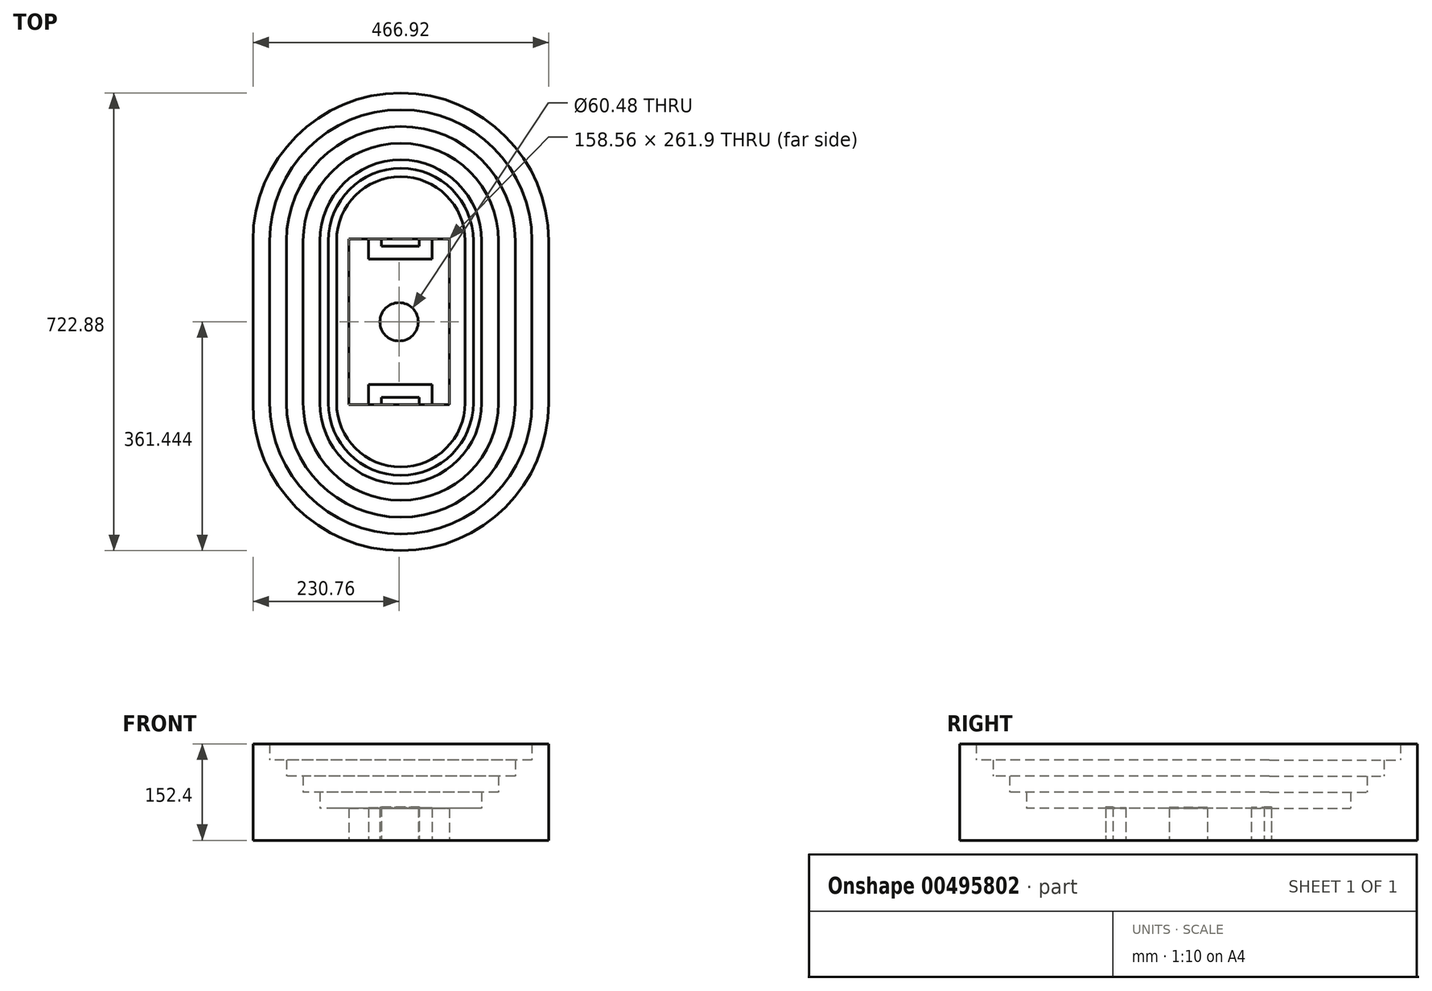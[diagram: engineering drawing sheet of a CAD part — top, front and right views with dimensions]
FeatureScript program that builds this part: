
annotation { "Feature Type Name" : "Feature", "Feature Type Description" : "" }
export const myFeature = defineFeature(function(context is Context, id is Id, definition is map)
    precondition{}
    {
        {
            var Q0;
            Q0=qCreatedBy(makeId("Top.planeOp"),FACE);
            var sketch = newSketch(context, id + "F0", { "sketchPlane" : qUnion([Q0])});
            skLineSegment(sketch, "E0.bottom", {"start": v(-59.16, 165.76) * mm, "end": v(99.4, 165.76) * mm});
            skLineSegment(sketch, "E0.top", {"start": v(-59.16, -96.14) * mm, "end": v(99.4, -96.14) * mm});
            skLineSegment(sketch, "E0.left", {"start": v(-59.16, 165.76) * mm, "end": v(-59.16, -96.14) * mm});
            skLineSegment(sketch, "E0.right", {"start": v(99.4, 165.76) * mm, "end": v(99.4, -96.14) * mm});
            skLineSegment(sketch, "E1.1", {"start": v(124.12, 162.8) * mm, "end": v(124.12, -93.16) * mm});
            skLineSegment(sketch, "E1.3", {"start": v(-78.49, 162.8) * mm, "end": v(-78.49, -93.16) * mm});
            skArc(sketch, "E2", {"start": v(124.12, 162.8) * mm, "mid": v(22.82, 264.1) * mm, "end": v(-78.49, 162.8) * mm});
            skArc(sketch, "E3", {"start": v(-78.49, -93.16) * mm, "mid": v(22.82, -194.47) * mm, "end": v(124.12, -93.16) * mm});
            skArc(sketch, "E4.0", {"start": v(137.34, 162.8) * mm, "mid": v(22.82, 277.31) * mm, "end": v(-91.7, 162.8) * mm});
            skLineSegment(sketch, "E4.1", {"start": v(137.34, 162.8) * mm, "end": v(137.34, -93.16) * mm});
            skArc(sketch, "E4.2", {"start": v(-91.7, -93.16) * mm, "mid": v(22.82, -207.68) * mm, "end": v(137.34, -93.16) * mm});
            skLineSegment(sketch, "E4.3", {"start": v(-91.7, 162.8) * mm, "end": v(-91.7, -93.16) * mm});
            skArc(sketch, "E5.0", {"start": v(150.55, 162.8) * mm, "mid": v(22.82, 290.53) * mm, "end": v(-104.92, 162.8) * mm});
            skLineSegment(sketch, "E5.1", {"start": v(150.55, 162.8) * mm, "end": v(150.55, -93.16) * mm});
            skArc(sketch, "E5.2", {"start": v(-104.92, -93.16) * mm, "mid": v(22.82, -220.9) * mm, "end": v(150.55, -93.16) * mm});
            skLineSegment(sketch, "E5.3", {"start": v(-104.92, 162.8) * mm, "end": v(-104.92, -93.16) * mm});
            skArc(sketch, "E6.0", {"start": v(176.98, 162.8) * mm, "mid": v(22.82, 316.96) * mm, "end": v(-131.35, 162.8) * mm});
            skLineSegment(sketch, "E6.1", {"start": v(176.98, 162.8) * mm, "end": v(176.98, -93.16) * mm});
            skArc(sketch, "E6.2", {"start": v(-131.35, -93.16) * mm, "mid": v(22.82, -247.33) * mm, "end": v(176.98, -93.16) * mm});
            skLineSegment(sketch, "E6.3", {"start": v(-131.35, 162.8) * mm, "end": v(-131.35, -93.16) * mm});
            skArc(sketch, "E7.0", {"start": v(203.42, 162.8) * mm, "mid": v(22.82, 343.4) * mm, "end": v(-157.78, 162.8) * mm});
            skLineSegment(sketch, "E7.1", {"start": v(203.42, 162.8) * mm, "end": v(203.42, -93.16) * mm});
            skArc(sketch, "E7.2", {"start": v(-157.78, -93.16) * mm, "mid": v(22.82, -273.76) * mm, "end": v(203.42, -93.16) * mm});
            skLineSegment(sketch, "E7.3", {"start": v(-157.78, 162.8) * mm, "end": v(-157.78, -93.16) * mm});
            skArc(sketch, "E8.0", {"start": v(229.85, 162.8) * mm, "mid": v(22.82, 369.82) * mm, "end": v(-184.21, 162.8) * mm});
            skLineSegment(sketch, "E8.1", {"start": v(229.85, 162.8) * mm, "end": v(229.85, -93.16) * mm});
            skArc(sketch, "E8.2", {"start": v(-184.21, -93.16) * mm, "mid": v(22.82, -300.2) * mm, "end": v(229.85, -93.16) * mm});
            skLineSegment(sketch, "E8.3", {"start": v(-184.21, 162.8) * mm, "end": v(-184.21, -93.16) * mm});
            skArc(sketch, "E9.0", {"start": v(256.28, 162.8) * mm, "mid": v(22.82, 396.25) * mm, "end": v(-210.64, 162.8) * mm});
            skLineSegment(sketch, "E9.1", {"start": v(256.28, 162.8) * mm, "end": v(256.28, -93.16) * mm});
            skArc(sketch, "E9.2", {"start": v(-210.64, -93.16) * mm, "mid": v(22.82, -326.63) * mm, "end": v(256.28, -93.16) * mm});
            skLineSegment(sketch, "E9.3", {"start": v(-210.64, 162.8) * mm, "end": v(-210.64, -93.16) * mm});
            skLineSegment(sketch, "E10", {"start": v(-59.16, 34.81) * mm, "end": v(99.4, 34.81) * mm});
            skCircle(sketch, "E11", {"center": v(20.12, 34.81) * mm, "radius": 30.24 * mm});
            skLineSegment(sketch, "E12", {"start": v(22.82, -96.14) * mm, "end": v(-27.98, -96.14) * mm});
            skLineSegment(sketch, "E13", {"start": v(22.82, -96.14) * mm, "end": v(67.85, -96.14) * mm});
            skLineSegment(sketch, "E14", {"start": v(-27.98, 165.76) * mm, "end": v(72.35, 165.76) * mm});
            skLineSegment(sketch, "E15", {"start": v(72.35, -96.14) * mm, "end": v(22.82, -96.14) * mm});
            skLineSegment(sketch, "E16", {"start": v(-27.98, -96.14) * mm, "end": v(-27.98, -64.39) * mm});
            skLineSegment(sketch, "E17", {"start": v(72.35, -96.14) * mm, "end": v(72.35, -64.39) * mm});
            skLineSegment(sketch, "E18", {"start": v(72.35, -64.39) * mm, "end": v(-27.98, -64.39) * mm});
            skLineSegment(sketch, "E19", {"start": v(-27.98, 165.76) * mm, "end": v(-27.98, 134.01) * mm});
            skLineSegment(sketch, "E20", {"start": v(-27.98, 134.01) * mm, "end": v(72.35, 134.01) * mm});
            skLineSegment(sketch, "E21", {"start": v(72.35, 134.01) * mm, "end": v(72.35, 165.76) * mm});
            skLineSegment(sketch, "E22.0", {"start": v(-7.66, -96.14) * mm, "end": v(-7.66, -84.7) * mm});
            skLineSegment(sketch, "E22.1", {"start": v(52.03, -84.7) * mm, "end": v(-7.66, -84.7) * mm});
            skLineSegment(sketch, "E22.2", {"start": v(52.03, -94.87) * mm, "end": v(52.03, -84.7) * mm});
            skLineSegment(sketch, "E23.0", {"start": v(52.03, 154.33) * mm, "end": v(52.03, 165.76) * mm});
            skLineSegment(sketch, "E23.1", {"start": v(-7.66, 154.33) * mm, "end": v(52.03, 154.33) * mm});
            skLineSegment(sketch, "E23.2", {"start": v(-7.66, 165.76) * mm, "end": v(-7.66, 154.33) * mm});
            skLineSegment(sketch, "E24", {"start": v(52.03, -94.87) * mm, "end": v(52.03, -96.14) * mm});
            skSolve(sketch);
        }
        {
            var Q0;
            {var subQ0=sQuery(id+"F0.wireOp",EDGE,"E23.0");Q0=makeQuery(id+"F0.imprint","IMPRINT",FACE,{"disambiguationData":[TD([[makeQuery(id+"F0.imprint","IMPRINT",EDGE,{"derivedFrom":subQ0}),1.0]])]});}
            var Q1;
            {var subQ0=sQuery(id+"F0.wireOp",EDGE,"E22.0");Q1=makeQuery(id+"F0.imprint","IMPRINT",FACE,{"disambiguationData":[TD([[makeQuery(id+"F0.imprint","IMPRINT",EDGE,{"derivedFrom":subQ0}),-1.0]])]});}
            extrude(context, id + "F1", {"entities" : qUnion([Q0, Q1]), "depth" : 53.34 * mm});
        }
        {
            var Q0;
            {var subQ0=sQuery(id+"F0.wireOp",EDGE,"E16");Q0=makeQuery(id+"F0.imprint","IMPRINT",FACE,{"disambiguationData":[TD([[makeQuery(id+"F0.imprint","IMPRINT",EDGE,{"derivedFrom":subQ0}),-1.0]])]});}
            var Q1;
            {var subQ0=sQuery(id+"F0.wireOp",EDGE,"E19");Q1=makeQuery(id+"F0.imprint","IMPRINT",FACE,{"disambiguationData":[TD([[makeQuery(id+"F0.imprint","IMPRINT",EDGE,{"derivedFrom":subQ0}),1.0]])]});}
            var Q2;
            {var subQ0=sQuery(id+"F0.wireOp",EDGE,"E11");var subQ1=sQuery(id+"F0.wireOp",EDGE,"E10");var subQ2=makeQuery(id+"F0.imprint","INTERSECT",VERTEX,{"disambiguationData":[OD(0.0)],"derivedFrom":[subQ1,subQ0]});Q2=makeQuery(id+"F0.imprint","IMPRINT",FACE,{"disambiguationData":[TD([[makeQuery(id+"F0.imprint","IMPRINT",EDGE,{"disambiguationData":[TD([[subQ2,-1.0]])],"derivedFrom":subQ1}),-1.0]])]});}
            var Q3;
            {var subQ0=sQuery(id+"F0.wireOp",EDGE,"E11");var subQ1=sQuery(id+"F0.wireOp",EDGE,"E10");var subQ2=makeQuery(id+"F0.imprint","INTERSECT",VERTEX,{"disambiguationData":[OD(0.0)],"derivedFrom":[subQ1,subQ0]});Q3=makeQuery(id+"F0.imprint","IMPRINT",FACE,{"disambiguationData":[TD([[makeQuery(id+"F0.imprint","IMPRINT",EDGE,{"disambiguationData":[TD([[subQ2,-1.0]])],"derivedFrom":subQ1}),1.0]])]});}
            extrude(context, id + "F2", {"entities" : qUnion([Q0, Q1, Q2, Q3]), "depth" : 52.07 * mm});
        }
        {
            var Q0;
            {var subQ13=sQuery(id+"F0.wireOp",EDGE,"E19");Q0=makeQuery(id+"F0.imprint","IMPRINT",FACE,{"disambiguationData":[TD([[makeQuery(id+"F0.imprint","IMPRINT",EDGE,{"derivedFrom":subQ13}),-1.0]])]});}
            var Q1;
            {var subQ9=sQuery(id+"F0.wireOp",EDGE,"E16");Q1=makeQuery(id+"F0.imprint","IMPRINT",FACE,{"disambiguationData":[TD([[makeQuery(id+"F0.imprint","IMPRINT",EDGE,{"derivedFrom":subQ9}),1.0]])]});}
            extrude(context, id + "F3", {"entities" : qUnion([Q0, Q1]), "depth" : 50.8 * mm});
        }
        {
            var Q0;
            Q0=makeQuery(id+"F0.imprint","IMPRINT",FACE,{"disambiguationData":[TD([[makeQuery(id+"F0.imprint","IMPRINT",EDGE,{"derivedFrom":sQuery(id+"F0.wireOp",EDGE,"E1.1")}),-1.0]])]});
            extrude(context, id + "F4", {"entities" : qUnion([Q0]), "depth" : 50.55 * mm});
        }
        {
            var Q0;
            Q0=makeQuery(id+"F0.imprint","IMPRINT",FACE,{"disambiguationData":[TD([[makeQuery(id+"F0.imprint","IMPRINT",EDGE,{"derivedFrom":sQuery(id+"F0.wireOp",EDGE,"E1.1")}),1.0]])]});
            extrude(context, id + "F5", {"entities" : qUnion([Q0]), "operationType" : NewBodyOperationType.ADD, "depth" : 50.77 * mm});
        }
        {
            var Q0;
            Q0=makeQuery(id+"F0.imprint","IMPRINT",FACE,{"disambiguationData":[TD([[makeQuery(id+"F0.imprint","IMPRINT",EDGE,{"derivedFrom":sQuery(id+"F0.wireOp",EDGE,"E4.0")}),-1.0]])]});
            extrude(context, id + "F6", {"entities" : qUnion([Q0]), "operationType" : NewBodyOperationType.ADD, "depth" : 50.8 * mm});
        }
        {
            var Q0;
            Q0=makeQuery(id+"F0.imprint","IMPRINT",FACE,{"disambiguationData":[TD([[makeQuery(id+"F0.imprint","IMPRINT",EDGE,{"derivedFrom":sQuery(id+"F0.wireOp",EDGE,"E5.0")}),-1.0]])]});
            extrude(context, id + "F7", {"entities" : qUnion([Q0]), "operationType" : NewBodyOperationType.ADD, "depth" : 76.2 * mm});
        }
        {
            var Q0;
            Q0=makeQuery(id+"F0.imprint","IMPRINT",FACE,{"disambiguationData":[TD([[makeQuery(id+"F0.imprint","IMPRINT",EDGE,{"derivedFrom":sQuery(id+"F0.wireOp",EDGE,"E6.0")}),-1.0]])]});
            extrude(context, id + "F8", {"entities" : qUnion([Q0]), "operationType" : NewBodyOperationType.ADD, "depth" : 101.6 * mm});
        }
        {
            var Q0;
            Q0=makeQuery(id+"F0.imprint","IMPRINT",FACE,{"disambiguationData":[TD([[makeQuery(id+"F0.imprint","IMPRINT",EDGE,{"derivedFrom":sQuery(id+"F0.wireOp",EDGE,"E7.0")}),-1.0]])]});
            extrude(context, id + "F9", {"entities" : qUnion([Q0]), "operationType" : NewBodyOperationType.ADD, "depth" : 127 * mm});
        }
        {
            var Q0;
            Q0=makeQuery(id+"F0.imprint","IMPRINT",FACE,{"disambiguationData":[TD([[makeQuery(id+"F0.imprint","IMPRINT",EDGE,{"derivedFrom":sQuery(id+"F0.wireOp",EDGE,"E8.0")}),-1.0]])]});
            extrude(context, id + "F10", {"entities" : qUnion([Q0]), "operationType" : NewBodyOperationType.ADD, "depth" : 152.4 * mm});
        }
    });
